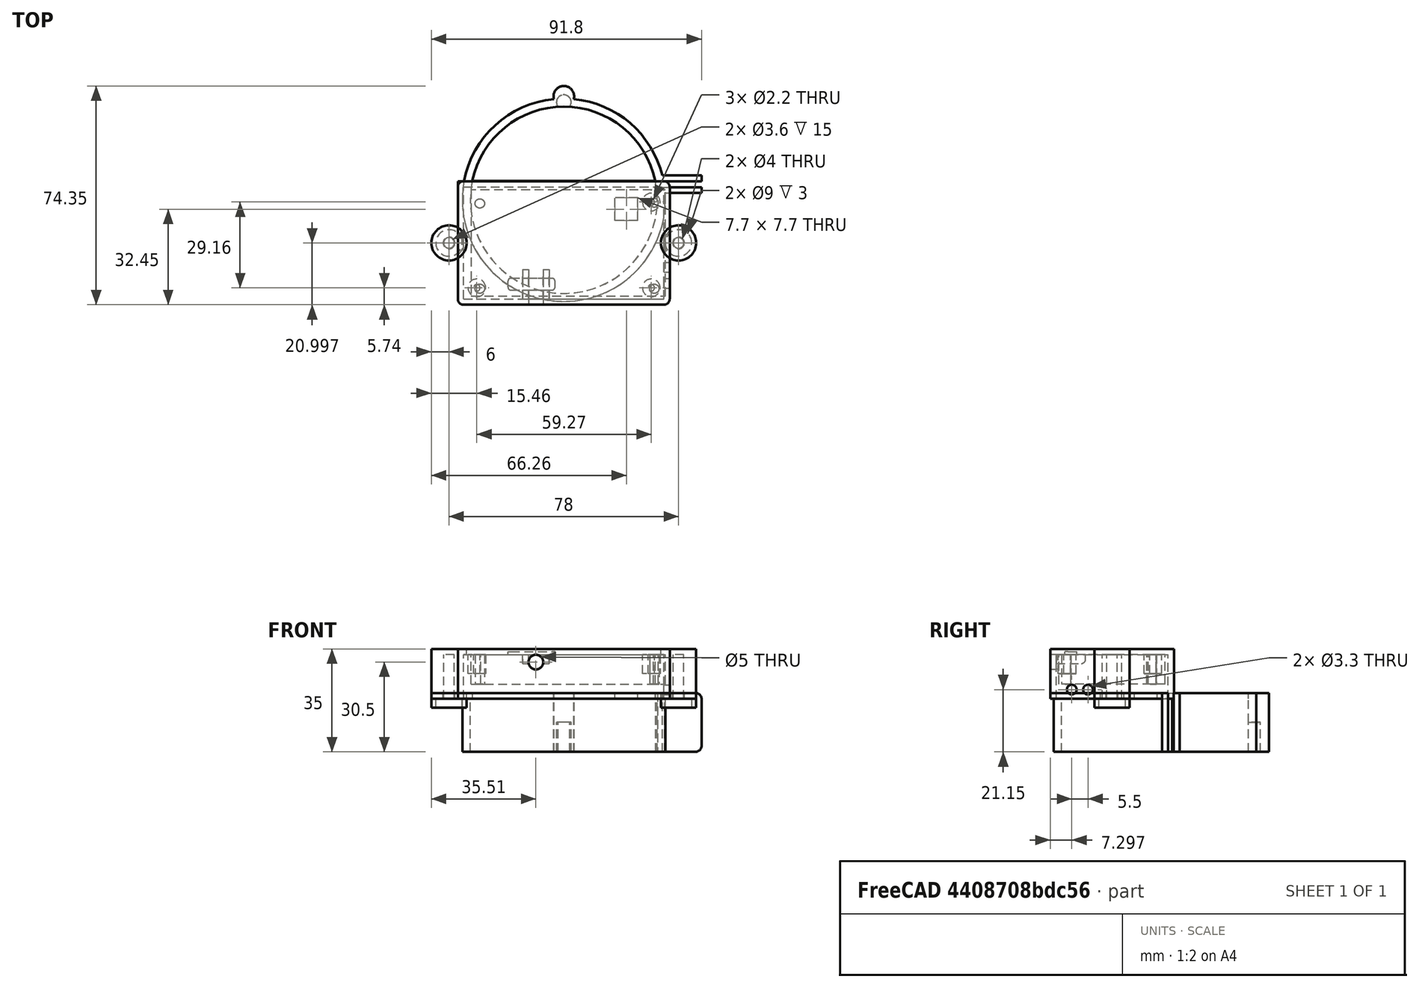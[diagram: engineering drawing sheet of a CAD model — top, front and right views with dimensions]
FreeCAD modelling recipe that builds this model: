
FCSTD DOCUMENT  (FreeCAD 0.18R4 (GitTag))
Label: CASE ver 2 in FreeCAD
License: All rights reserved
LicenseURL: http://en.wikipedia.org/wiki/All_rights_reserved
objects: Part::Cylinder×24, Part::Cut×20, Part::Box×15, Part::MultiFuse×13, Part::Extrusion×12, Part::Part2DObjectPython×8, Part::Fillet×7, Part::Feature×4, Part::Fuse×2
note: 105 computed .brp shape members not serialized (recipe doc carries the construction recipe); baked Part::Feature solids carry a one-line shape summary decoded from their .brp

FEATURE [Part::Cylinder] Cylinder
  Angle = 360
  AttacherType = Attacher::AttachEngine3D
  Height = 18
  Radius = 31.75
FEATURE [Part::Cylinder] Cylinder001
  Angle = 360
  AttacherType = Attacher::AttachEngine3D
  Height = 20
  Radius = 34.5
FEATURE [Part::Cylinder] Cylinder002
  Angle = 360
  AttacherType = Attacher::AttachEngine3D
  Height = 25
  Radius = 31.75
FEATURE [Part::Box] Box  label="Kostka"
  AttacherType = Attacher::AttachEngine3D
  Height = 25
  Length = 80
  Placement = pos=(-38,-32.5,0) rot=(0,0,1;0rad)
  Width = 39
FEATURE [Part::Box] Box001  label="Kostka001"
  AttacherType = Attacher::AttachEngine3D
  Height = 10
  Length = 7.7
  Placement = pos=(25.1,-7,10) rot=(0,0,1;1.5708rad)
  Width = 7.7
FEATURE [Part::Box] Box002  label="Kostka002"
  AttacherType = Attacher::AttachEngine3D
  Height = 20
  Length = 10
  Placement = pos=(31.2216,4.36291,0) rot=(0,0,1;0rad)
  Width = 2
FEATURE [Part::Box] Box005  label="Kostka005"
  AttacherType = Attacher::AttachEngine3D
  Height = 20
  Length = 15
  Placement = pos=(31.79,6.35995,0) rot=(0,0,1;0rad)
  Width = 2
FEATURE [Part::Box] Box006  label="Kostka006"
  AttacherType = Attacher::AttachEngine3D
  Height = 20
  Length = 15
  Placement = pos=(31.7936,2.35995,0) rot=(0,0,1;0rad)
  Width = 2
FEATURE [Part::Box] Box007  label="Kostka007"
  AttacherType = Attacher::AttachEngine3D
  Height = 2
  Length = 72
  Placement = pos=(-36.01,-35.6034,18) rot=(0,0,1;0rad)
  Width = 42
FEATURE [Part::Cut] Cut
  Base = -> Cylinder001
  Tool = -> Cylinder
FEATURE [Part::Cut] Cut001
  Base = -> Cylinder002
  Tool = -> Box
FEATURE [Part::MultiFuse] Fusion
  Shapes = -> [Cut,Box007]
FEATURE [Part::Cut] Cut002
  Base = -> Fusion
  Tool = -> Box001
FEATURE [Part::Cut] Cut003
  Base = -> Cut002
  Tool = -> Cut001
FEATURE [Part::Cut] Cut004
  Base = -> Cut003
  Tool = -> Box002
FEATURE [Part::Box] Box008  label="Kostka008"
  AttacherType = Attacher::AttachEngine3D
  Height = 17
  Length = 72
  Placement = pos=(-36.01,-35.6034,18) rot=(0,0,1;0rad)
  Width = 42
FEATURE [Part::Box] Box009  label="Kostka009"
  AttacherType = Attacher::AttachEngine3D
  Height = 15
  Length = 68
  Placement = pos=(-34.01,-33.6034,18) rot=(0,0,1;0rad)
  Width = 38
FEATURE [Part::Fillet] Fillet001
  Base = -> Cut004
  Edges = 2 edges r=2: [Edge1,Edge6]
FEATURE [Part::Fillet] Fillet002
  Base = -> Box005
  Edges = 2 edges r=2: [Edge6,Edge8]
FEATURE [Part::Fillet] Fillet003
  Base = -> Box006
  Edges = 2 edges r=2: [Edge6,Edge8]
FEATURE [Part::Fuse] Fusion001
  Base = -> Fillet001
  Tool = -> Fillet002
FEATURE [Part::Fuse] Fusion002  label="PODST"
  Base = -> Fillet003
  Tool = -> Fusion001
FEATURE [Part::Cut] Cut005
  Base = -> Box008
  Tool = -> Box009
FEATURE [Part::Fillet] Fillet  label="POKRYWA_1"
  Base = -> Cut005
  Edges = 4 edges r=2: [Edge1,Edge3,Edge6,Edge11]
FEATURE [Part::Part2DObjectPython] Circle001  # Draft 2D object (typed FeaturePython)
  FirstAngle = 0
  LastAngle = 0
  MakeFace = false
  Placement = pos=(130.06,-64.7857,0) rot=(0,0,1;0rad)
  Radius = 0.5
FEATURE [Part::Part2DObjectPython] Circle002  # Draft 2D object (typed FeaturePython)
  FirstAngle = 0
  LastAngle = 0
  MakeFace = false
  Placement = pos=(70.7984,-64.7696,0) rot=(0,0,1;0rad)
  Radius = 0.5
FEATURE [Part::Part2DObjectPython] Circle  # Draft 2D object (typed FeaturePython)
  FirstAngle = 0
  LastAngle = 0
  MakeFace = false
  Placement = pos=(130.059,-35.5556,0) rot=(0,0,1;0rad)
  Radius = 0.5
FEATURE [Part::Part2DObjectPython] Rectangle  # Draft 2D object (typed FeaturePython)
  ChamferSize = 0
  Columns = 1
  FilletRadius = 0
  Height = 36
  Length = 66
  MakeFace = false
  Placement = pos=(67.8363,-67.2127,0) rot=(0,0,1;0rad)
  Rows = 1
FEATURE [Part::Part2DObjectPython] Circle003  # Draft 2D object (typed FeaturePython)
  FirstAngle = 0
  LastAngle = 0
  MakeFace = false
  Placement = pos=(70.7901,-35.8008,0) rot=(0,0,1;0rad)
  Radius = 0.5
FEATURE [Part::Extrusion] Extrude093
  Base = -> Circle
  Dir = (0,0,1)
  DirMode = 0
  FaceMakerClass = Part::FaceMakerBullseye
  LengthFwd = 10
  LengthRev = 0
  Solid = true
  Symmetric = false
FEATURE [Part::Extrusion] Extrude095
  Base = -> Circle002
  Dir = (0,0,1)
  DirMode = 0
  FaceMakerClass = Part::FaceMakerBullseye
  LengthFwd = 10
  LengthRev = 0
  Solid = true
  Symmetric = false
FEATURE [Part::Extrusion] Extrude096
  Base = -> Circle003
  Dir = (0,0,1)
  DirMode = 0
  FaceMakerClass = Part::FaceMakerBullseye
  LengthFwd = 10
  LengthRev = 0
  Solid = true
  Symmetric = false
FEATURE [Part::Extrusion] Extrude094
  Base = -> Circle001
  Dir = (0,0,1)
  DirMode = 0
  FaceMakerClass = Part::FaceMakerBullseye
  LengthFwd = 10
  LengthRev = 0
  Solid = true
  Symmetric = false
FEATURE [Part::Extrusion] Extrude097
  Base = -> Rectangle
  Dir = (0,0,1)
  DirMode = 0
  FaceMakerClass = Part::FaceMakerBullseye
  LengthFwd = 10
  LengthRev = 0
  Solid = true
  Symmetric = false
FEATURE [Part::MultiFuse] Fusion003  label="PCB"
  Placement = pos=(-99.3416,34.6093,23) rot=(0,0,1;0rad)
  Shapes = -> [Extrude093,Extrude094,Extrude095,Extrude096,Extrude097]
FEATURE [Part::Feature] path847010
  shape: bbox 3.193 x 3.179 x 2e-07 mm, 1 faces, 0 solids (baked)
FEATURE [Part::Feature] path847007
  shape: bbox 2.86 x 2.857 x 2e-07 mm, 1 faces, 0 solids (baked)
FEATURE [Part::Feature] path847090
  shape: bbox 3.193 x 3.187 x 2e-07 mm, 1 faces, 0 solids (baked)
FEATURE [Part::Feature] path847092
  shape: bbox 3.193 x 3.187 x 2e-07 mm, 1 faces, 0 solids (baked)
FEATURE [Part::Extrusion] Extrude005
  Base = -> path847007
  Dir = (0,0,1)
  DirMode = 0
  FaceMakerClass = Part::FaceMakerBullseye
  LengthFwd = 10
  LengthRev = 0
  Solid = false
  Symmetric = false
FEATURE [Part::Extrusion] Extrude008
  Base = -> path847010
  Dir = (0,0,1)
  DirMode = 0
  FaceMakerClass = Part::FaceMakerBullseye
  LengthFwd = 10
  LengthRev = 0
  Solid = false
  Symmetric = false
FEATURE [Part::Extrusion] Extrude090
  Base = -> path847092
  Dir = (0,0,1)
  DirMode = 0
  FaceMakerClass = Part::FaceMakerBullseye
  LengthFwd = 10
  LengthRev = 0
  Solid = false
  Symmetric = false
FEATURE [Part::Extrusion] Extrude088
  Base = -> path847090
  Dir = (0,0,1)
  DirMode = 0
  FaceMakerClass = Part::FaceMakerBullseye
  LengthFwd = 10
  LengthRev = 0
  Solid = false
  Symmetric = false
FEATURE [Part::MultiFuse] Fusion004  label="PCB_HOLES"
  Placement = pos=(-99.3416,34.6093,23) rot=(0,0,1;0rad)
  Shapes = -> [Extrude008,Extrude088,Extrude005,Extrude090]
FEATURE [Part::Part2DObjectPython] Circle004  # Draft 2D object (typed FeaturePython)
  FirstAngle = 0
  LastAngle = 0
  MakeFace = false
  Placement = pos=(-28.5503,-30.1605,33) rot=(1,0,0;3.14159rad)
  Radius = 3
FEATURE [Part::Part2DObjectPython] Circle006  # Draft 2D object (typed FeaturePython)
  FirstAngle = 0
  LastAngle = 0
  MakeFace = false
  Placement = pos=(30.7196,-1,33) rot=(1,0,0;3.14159rad)
  Radius = 3
FEATURE [Part::Part2DObjectPython] Circle007  # Draft 2D object (typed FeaturePython)
  FirstAngle = 0
  LastAngle = 0
  MakeFace = false
  Placement = pos=(30.7196,-30.1605,33) rot=(1,0,0;3.14159rad)
  Radius = 3
FEATURE [Part::Extrusion] Extrude
  Base = -> Circle004
  Dir = (0,0,-1)
  DirMode = 0
  FaceMakerClass = Part::FaceMakerBullseye
  LengthFwd = 6.5
  LengthRev = 0
  Solid = true
  Symmetric = false
FEATURE [Part::Extrusion] Extrude099
  Base = -> Circle006
  Dir = (0,0,-1)
  DirMode = 0
  FaceMakerClass = Part::FaceMakerBullseye
  LengthFwd = 6.5
  LengthRev = 0
  Solid = true
  Symmetric = false
FEATURE [Part::Extrusion] Extrude100
  Base = -> Circle007
  Dir = (0,0,-1)
  DirMode = 0
  FaceMakerClass = Part::FaceMakerBullseye
  LengthFwd = 6.5
  LengthRev = 0
  Solid = true
  Symmetric = false
FEATURE [Part::MultiFuse] Fusion005
  Shapes = -> [Extrude,Extrude099,Extrude100]
FEATURE [Part::Cylinder] Cylinder003
  Angle = 360
  AttacherType = Attacher::AttachEngine3D
  Height = 6.5
  Placement = pos=(-28.5503,-1,26.5) rot=(0,0,1;0rad)
  Radius = 1.1
FEATURE [Part::Cylinder] Cylinder004
  Angle = 360
  AttacherType = Attacher::AttachEngine3D
  Height = 6.5
  Placement = pos=(-28.5503,-30.1605,26.5) rot=(0,0,1;0rad)
  Radius = 1.1
FEATURE [Part::Cylinder] Cylinder005
  Angle = 360
  AttacherType = Attacher::AttachEngine3D
  Height = 6.5
  Placement = pos=(30.7196,-30.1605,26.5) rot=(0,0,1;0rad)
  Radius = 1.1
FEATURE [Part::Cylinder] Cylinder006
  Angle = 360
  AttacherType = Attacher::AttachEngine3D
  Height = 6.5
  Placement = pos=(30.7196,-1,26.5) rot=(0,0,1;0rad)
  Radius = 1.1
FEATURE [Part::MultiFuse] Fusion006
  Shapes = -> [Cylinder003,Cylinder006,Cylinder005,Cylinder004]
FEATURE [Part::Cut] Cut006  label="PCB MOUNT"
  Base = -> Fusion005
  Placement = pos=(-1,0.3,0) rot=(0,0,1;0rad)
  Tool = -> Fusion006
FEATURE [Part::Cylinder] Cylinder010
  Angle = 360
  AttacherType = Attacher::AttachEngine3D
  Height = 5
  Placement = pos=(-39.01,-14.6034,15) rot=(0,0,1;0rad)
  Radius = 6
FEATURE [Part::Cylinder] Cylinder011
  Angle = 360
  AttacherType = Attacher::AttachEngine3D
  Height = 5
  Placement = pos=(-39.01,-14.6034,15) rot=(0,0,1;0rad)
  Radius = 2
FEATURE [Part::Cylinder] Cylinder012
  Angle = 360
  AttacherType = Attacher::AttachEngine3D
  Height = 3
  Placement = pos=(-39.01,-14.6034,15) rot=(0,0,1;0rad)
  Radius = 4.5
FEATURE [Part::Cut] Cut009
  Base = -> Cylinder010
  Tool = -> Cylinder012
FEATURE [Part::Cut] Cut010
  Base = -> Cut009
  Tool = -> Cylinder011
FEATURE [Part::Cylinder] Cylinder013
  Angle = 360
  AttacherType = Attacher::AttachEngine3D
  Height = 3
  Placement = pos=(-39.01,-14.6034,15) rot=(0,0,1;0rad)
  Radius = 4.5
FEATURE [Part::Cylinder] Cylinder014
  Angle = 360
  AttacherType = Attacher::AttachEngine3D
  Height = 5
  Placement = pos=(-39.01,-14.6034,15) rot=(0,0,1;0rad)
  Radius = 2
FEATURE [Part::Box] Box011  label="Kostka011"
  AttacherType = Attacher::AttachEngine3D
  Height = 17
  Length = 5
  Placement = pos=(-39.01,-17.1034,18) rot=(0,0,1;0rad)
  Width = 5
FEATURE [Part::Cylinder] Cylinder016
  Angle = 360
  AttacherType = Attacher::AttachEngine3D
  Height = 15
  Placement = pos=(-39.01,-14.6034,18) rot=(0,0,1;0rad)
  Radius = 1.8
FEATURE [Part::Cylinder] Cylinder017
  Angle = 360
  AttacherType = Attacher::AttachEngine3D
  Height = 17
  Placement = pos=(-39.01,-14.6034,18) rot=(0,0,1;0rad)
  Radius = 6
FEATURE [Part::Cylinder] Cylinder018
  Angle = 360
  AttacherType = Attacher::AttachEngine3D
  Height = 5
  Placement = pos=(-39.01,-14.6034,15) rot=(0,0,1;0rad)
  Radius = 6
FEATURE [Part::Cut] Cut011
  Base = -> Cylinder018
  Tool = -> Cylinder013
FEATURE [Part::Cut] Cut012
  Base = -> Cut011
  Placement = pos=(-0.02,-29.2068,0) rot=(0,0,1;3.14159rad)
  Tool = -> Cylinder014
FEATURE [Part::Cylinder] Cylinder019
  Angle = 360
  AttacherType = Attacher::AttachEngine3D
  Height = 5
  Placement = pos=(38.99,-14.6034,15) rot=(0,0,1;0rad)
  Radius = 5
FEATURE [Part::Cylinder] Cylinder020
  Angle = 360
  AttacherType = Attacher::AttachEngine3D
  Height = 5
  Placement = pos=(-39.01,-14.6034,15) rot=(0,0,1;0rad)
  Radius = 5
FEATURE [Part::MultiFuse] Fusion013
  Shapes = -> [Cylinder019,Cylinder020]
FEATURE [Part::Cut] Cut015  label="BASE_001"
  Base = -> Fusion002
  Tool = -> Fusion013
FEATURE [Part::Cylinder] Cylinder021
  Angle = 360
  AttacherType = Attacher::AttachEngine3D
  Height = 17
  Placement = pos=(38.99,-14.6034,18) rot=(0,0,1;0rad)
  Radius = 6
FEATURE [Part::Box] Box012  label="Kostka012"
  AttacherType = Attacher::AttachEngine3D
  Height = 17
  Length = 5
  Placement = pos=(34.0681,-17.1,18) rot=(0,0,1;0rad)
  Width = 5
FEATURE [Part::Cylinder] Cylinder022
  Angle = 360
  AttacherType = Attacher::AttachEngine3D
  Height = 15
  Placement = pos=(38.99,-14.6034,18) rot=(0,0,1;0rad)
  Radius = 1.8
FEATURE [Part::MultiFuse] Fusion012  label="BASE MOUNT"
  Shapes = -> [Cut012,Cut010]
FEATURE [Part::MultiFuse] Fusion014
  Shapes = -> [Box011,Cylinder017]
FEATURE [Part::MultiFuse] Fusion015
  Shapes = -> [Box012,Cylinder021]
FEATURE [Part::Cut] Cut016
  Base = -> Fusion014
  Tool = -> Cylinder016
FEATURE [Part::Cut] Cut017
  Base = -> Fusion015
  Tool = -> Cylinder022
FEATURE [Part::Box] Box013  label="Kostka013"
  AttacherType = Attacher::AttachEngine3D
  Height = 15
  Length = 10
  Placement = pos=(-34.01,-19.6034,18) rot=(0,0,1;0rad)
  Width = 10
FEATURE [Part::Box] Box014  label="Kostka014"
  AttacherType = Attacher::AttachEngine3D
  Height = 15
  Length = 10
  Placement = pos=(23.99,-19.6034,18) rot=(0,0,1;0rad)
  Width = 10
FEATURE [Part::Cut] Cut018
  Base = -> Cut016
  Tool = -> Box013
FEATURE [Part::Cut] Cut019
  Base = -> Cut017
  Tool = -> Box014
FEATURE [Part::MultiFuse] Fusion016  label="COVER MOUNT"
  Shapes = -> [Cut018,Cut019]
FEATURE [Part::Cylinder] Cylinder023
  Angle = 360
  AttacherType = Attacher::AttachEngine3D
  Height = 2
  Placement = pos=(-9.5,-33.6034,30.5) rot=(1,0,0;1.5708rad)
  Radius = 2.5
FEATURE [Part::Box] Box015  label="Kostka015"
  AttacherType = Attacher::AttachEngine3D
  Height = 5
  Length = 2
  Placement = pos=(-14,-33.6,30) rot=(0,0,1;0rad)
  Width = 10
FEATURE [Part::Box] Box017  label="Kostka017"
  AttacherType = Attacher::AttachEngine3D
  Height = 1
  Length = 16
  Placement = pos=(-19,-30.6,33) rot=(0,0,1;0rad)
  Width = 4
FEATURE [Part::Box] Box018  label="Kostka018"
  AttacherType = Attacher::AttachEngine3D
  Height = 5
  Length = 2
  Placement = pos=(-7,-33.6,30) rot=(0,0,1;0rad)
  Width = 10
FEATURE [Part::Cut] Cut020
  Base = -> Fillet
  Tool = -> Cylinder023
FEATURE [Part::Fillet] Fillet004
  Base = -> Box017
  Edges = 4 edges r=1: [Edge1,Edge3,Edge5,Edge7]
FEATURE [Part::Fillet] Fillet005
  Base = -> Box018
  Edges = 1 edges r=1.5: [Edge11]
FEATURE [Part::Fillet] Fillet006
  Base = -> Box015
  Edges = 1 edges r=1.5: [Edge11]
FEATURE [Part::MultiFuse] Fusion017
  Shapes = -> [Fillet005,Fillet006,Cut020]
FEATURE [Part::Cylinder] Cylinder024
  Angle = 360
  AttacherType = Attacher::AttachEngine3D
  Height = 10
  Placement = pos=(33.99,-28.3034,21.15) rot=(0,1,0;1.5708rad)
  Radius = 1.65
FEATURE [Part::Cylinder] Cylinder025
  Angle = 360
  AttacherType = Attacher::AttachEngine3D
  Height = 10
  Placement = pos=(33.99,-22.8034,21.15) rot=(0,1,0;1.5708rad)
  Radius = 1.65
FEATURE [Part::MultiFuse] Fusion018
  Shapes = -> [Cylinder024,Cylinder025]
FEATURE [Part::Cut] Cut021
  Base = -> Fusion017
  Tool = -> Fusion018
FEATURE [Part::Cut] Cut022  label="COVER"
  Base = -> Cut021
  Tool = -> Fillet004
FEATURE [Part::Cylinder] Cylinder026
  Angle = 360
  AttacherType = Attacher::AttachEngine3D
  Height = 20
  Placement = pos=(-4e-16,35.25,0) rot=(0,0,1;0rad)
  Radius = 3.5
FEATURE [Part::Cylinder] Cylinder027
  Angle = 360
  AttacherType = Attacher::AttachEngine3D
  Height = 10
  Placement = pos=(2e-16,33.25,0) rot=(0,0,1;0rad)
  Radius = 2.5
FEATURE [Part::MultiFuse] Fusion019
  Shapes = -> [Cylinder026,Cut015]
FEATURE [Part::Cut] Cut023  label="BASE"
  Base = -> Fusion019
  Tool = -> Cylinder027
